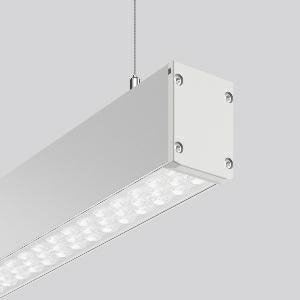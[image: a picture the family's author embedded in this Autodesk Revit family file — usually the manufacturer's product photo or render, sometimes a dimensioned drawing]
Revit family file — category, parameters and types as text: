
# Revit family: linedo_single_ip54_312566_000_1_76_2314
name_source: partatom
category: Lighting Fixtures
units: mm (PartAtom-declared; Revit-internal decimal feet)

## family parameters
Cut with Voids When Loaded = No
Host = Face
Light Source = No
Part Type = Normal
Room Calculation Point = No
Round Connector Dimension = Use Diameter
Shared = No

## types (1)
- LINEDO single IP54 (1 x LED Modul 840, 6450 lm, 4000)
    Apparent Load = 40 VA
    CIE Flux Codes = 86 96 99 100 100
    Color Rendering = 80
    Color Temperature = 4000
    Default Elevation = 1800 mm
    Description = Series: LINEDO single IP54
Stylish pendant luminaire. High-efficiency LED units with optimum light control thanks to clear plastic (PC) lens optics. 2-point steel cable suspension freely positionable and infinitely height-adjustable. With power cord (2.5 m). Please order canopy separately if required. Perfect for office areas (RUG < 19) and environments with computer screens in accordance with EN 12464-1. Luminaire with limited surface temperature in accordance with EN 60598-2-24 for use in environments in which a deposit of conductive dust on the luminaire can be expected. 
Colour: anodised aluminium
Length: 2274 mm
Width: 58 mm
Height: 76 mm
Suspension length: 100-1500 mm
Lamp: LED
Socket: without socket
Colour temperature: 4000K
Colour rendering index (CRI): 80
System power: 40 W
Rated luminous flux: 6450 lm
Beam angle Down: 59°
Luminous efficiency: 161 lm/W
Control gear: Converter, dimmable, DALI
Protection class: I
Type of protection: IP 54
    Height = 76 mm
    Lamp = 1 x LED Modul 840
    Lamp Light Flux = 6450 lm
    Lamp count = 1
    Length = 2274 mm
    Lifetime = 50000 h
    Luminous efficacy = 161 lm/W
    Manufacturer = RZB
    ModVariant = No
    Model = 312566.000.1.76
    Mounting Place = Ceiling
    Mounting Type = Pendant
    Number of Poles = 1
    OnlyDefault = Yes
    Power Factor = 1
    Product Name = LINEDO single IP54
    Product group = Pendant luminaires
    ProductGroupID = 902
    Protection Class = Protection class I
    Protection Degree = Degree of protection
    RLX_Detail_Level = 1
    RLX_Emergency_Light_Flux = 0 lm
    RLX_Emergency_Type = 0
    RLX_Emergency_Type_DB = No
    RlxData = <blob elided: 30765 chars, md5=6850acc9>
    Socket = socket
    Standby Power = 0 W
    System Light Flux = 6450 lm
    System Power = 40 W
    Type Comments = ALEA SPOT
    Type Image = 312565.000.jpg
    URL = http://relux.com
    VarID = ---
    Voltage = 0 V
    Weight = 0.00 kg
    Width = 58 mm

## geometry (parser evidence)
native form markers: Blend x4, Sweep x10
no freeform markers — native parametric forms only
